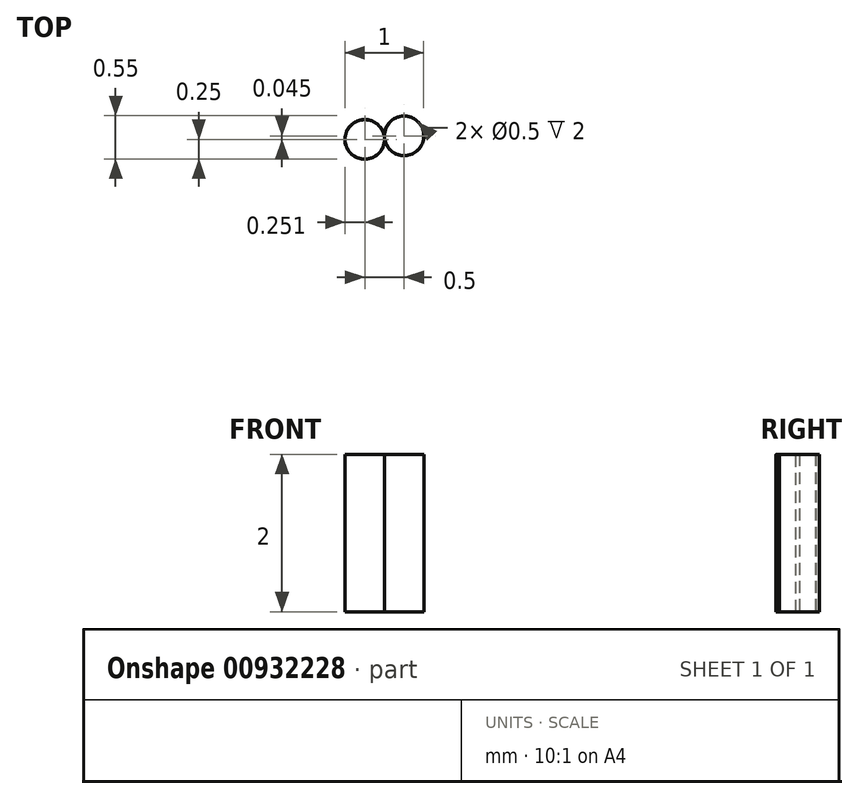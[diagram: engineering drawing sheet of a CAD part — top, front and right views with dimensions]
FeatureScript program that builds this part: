
annotation { "Feature Type Name" : "Feature", "Feature Type Description" : "" }
export const myFeature = defineFeature(function(context is Context, id is Id, definition is map)
    precondition{}
    {
        {
            var Q0;
            Q0=qCreatedBy(makeId("Top.planeOp"),FACE);
            var sketch = newSketch(context, id + "F0", { "sketchPlane" : qUnion([Q0])});
            skCircle(sketch, "E0", {"center": v(10.91, 7.17) * mm, "radius": 0.25 * mm});
            skCircle(sketch, "E1", {"center": v(11.41, 7.21) * mm, "radius": 0.25 * mm});
            skSolve(sketch);
        }
        {
            var Q0;
            Q0 = qSketchRegion(id + "F0", true);
            extrude(context, id + "F1", {"entities" : qUnion([Q0]), "depth" : 2 * mm, "offsetDistance" : 25 * mm});
        }
    });
